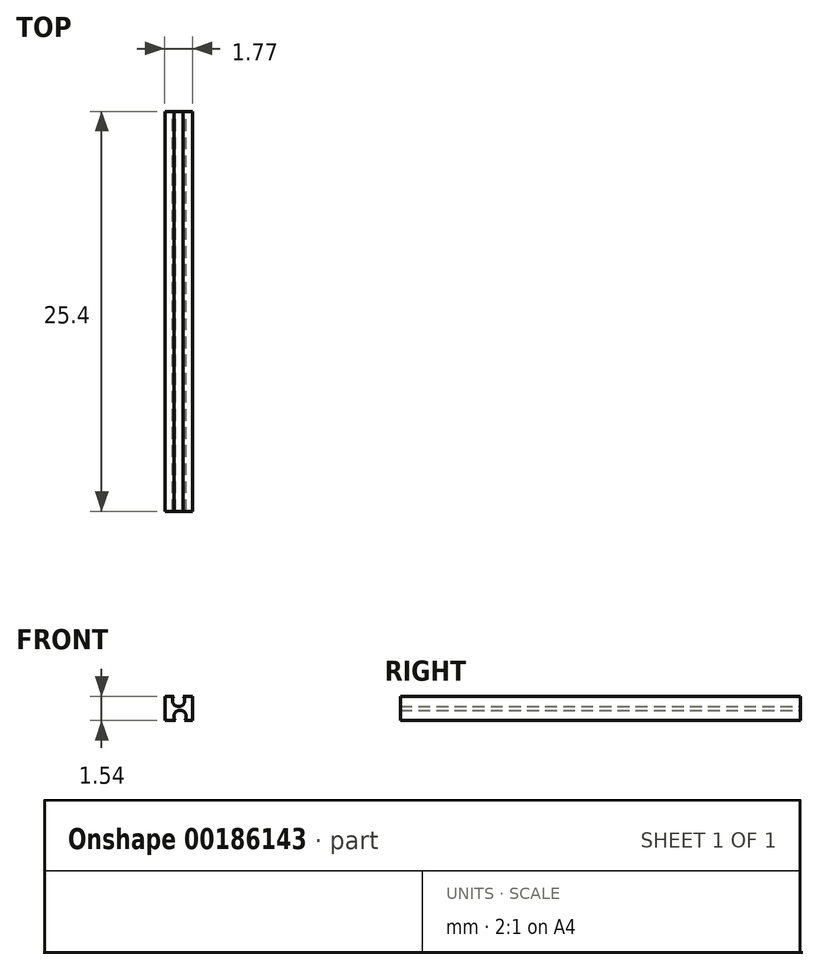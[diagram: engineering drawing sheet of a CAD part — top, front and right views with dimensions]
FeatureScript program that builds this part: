
annotation { "Feature Type Name" : "Feature", "Feature Type Description" : "" }
export const myFeature = defineFeature(function(context is Context, id is Id, definition is map)
    precondition{}
    {
        {
            var Q0;
            Q0=qCreatedBy(makeId("Front.planeOp"),FACE);
            var sketch = newSketch(context, id + "F0", { "sketchPlane" : qUnion([Q0])});
            skPoint(sketch, "E0.middle", {"position": v(0, 0) * mm});
            skCircle(sketch, "E1", {"center": v(-0.1, 0.51) * mm, "radius": 0.4 * mm});
            skPoint(sketch, "E1.centerSnap0", {"position": v(-0.1, 0.77) * mm});
            skCircle(sketch, "E2", {"center": v(0, -0.52) * mm, "radius": 0.4 * mm});
            skPoint(sketch, "E2.centerSnap0", {"position": v(0, -0.77) * mm});
            skLineSegment(sketch, "E3", {"start": v(-0.1, 0.77) * mm, "end": v(0.8, 0.77) * mm});
            skLineSegment(sketch, "E4", {"start": v(-0.1, 0.77) * mm, "end": v(-0.97, 0.77) * mm});
            skLineSegment(sketch, "E5", {"start": v(-0.94, -0.77) * mm, "end": v(0.8, -0.77) * mm});
            skLineSegment(sketch, "E6", {"start": v(0.8, 0.77) * mm, "end": v(0.8, -0.77) * mm});
            skLineSegment(sketch, "E7", {"start": v(-0.97, 0.77) * mm, "end": v(-0.94, -0.77) * mm});
            skSolve(sketch);
        }
        {
            var Q0;
            {var subQ4=sQuery(id+"F0.wireOp",EDGE,"E6");Q0=makeQuery(id+"F0.imprint","IMPRINT",FACE,{"disambiguationData":[TD([[makeQuery(id+"F0.imprint","IMPRINT",EDGE,{"derivedFrom":subQ4}),-1.0]])]});}
            extrude(context, id + "F1", {"entities" : qUnion([Q0]), "depth" : 25.4 * mm});
        }
    });
